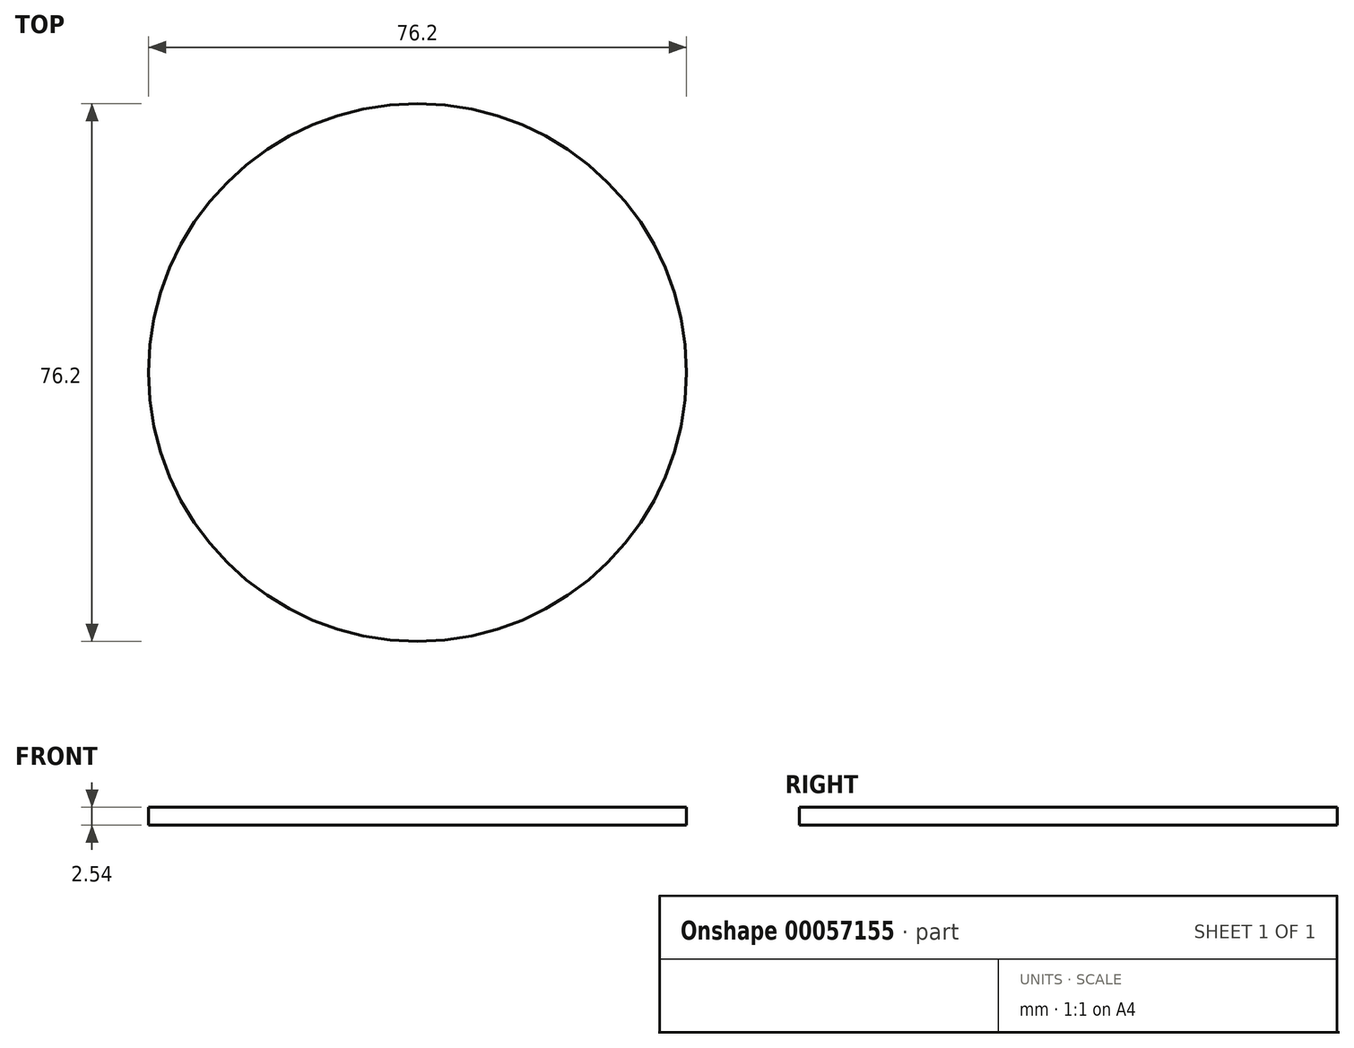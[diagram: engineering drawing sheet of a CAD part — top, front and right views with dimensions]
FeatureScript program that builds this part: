
annotation { "Feature Type Name" : "Feature", "Feature Type Description" : "" }
export const myFeature = defineFeature(function(context is Context, id is Id, definition is map)
    precondition{}
    {
        {
            var Q0;
            Q0=qCreatedBy(makeId("Top.planeOp"),FACE);
            var sketch = newSketch(context, id + "F0", { "sketchPlane" : qUnion([Q0])});
            skCircle(sketch, "E0", {"center": v(0, 0) * mm, "radius": 38.1 * mm});
            skSolve(sketch);
        }
        {
            var Q0;
            Q0=makeQuery(id+"F0.imprint","IMPRINT",FACE,{"disambiguationData":[TD([[makeQuery(id+"F0.imprint","IMPRINT",EDGE,{"derivedFrom":sQuery(id+"F0.wireOp",EDGE,"E0")}),1.0]])]});
            extrude(context, id + "F1", {"entities" : qUnion([Q0]), "depth" : 2.54 * mm});
        }
    });
